# Revit family: KORO
name_source: partatom
category: Luminaires
units: mm (PartAtom-declared; Revit-internal decimal feet)

## family parameters
Cote de connecteur circulaire = Utiliser le diamètre
Couper avec des vides une fois chargée = Oui
Hôte = Face
Numéro OmniClass = 23.80.70.11.17
Partagée = Non
Point de calcul de pièce = Oui
Source d'éclairage = Oui
Titre OmniClass = Specialized Lighting by Location or Use
Type d'élément = Normal

## types (1)
- 621400
    Angle de l'inclinaison = 60.00°
    Charge apparente = 38 VA
    Commentaires relatifs à la puissance = 36.5W
    Coût = 167.5 $
    Description = Encastré tertiaire équipé de platines LED, efficacité lumineuse de 133.8lm/W
    Distance bord corps = 24 mm  [stored 0.0787402 ft]
    Distance diffuseur/diffuseur = 24 mm  [stored 0.0787402 ft]
    Elévation par défaut = 0 mm  [stored 0 ft]
    Emettre à partir de la longueur de la ligne = 610 mm
    Fabricant = Résistex
    Fichier de distribution photométrique = 621400.ies
    Filtre de couleur = 16777215
    Garantie = 5 ans
    Gradation des changements de température de couleur de lampe = <Aucun>
    IK = 04
    IP = 40
    Image du type = <Aucun>
    Indice de charge = Eclairage
    Largeur = 295 mm  [stored 0.967848 ft]
    Largeur diffuseur = 79 mm  [stored 0.259186 ft]
    Longueur = 1195 mm  [stored 3.9206 ft]
    Longueur diffuseur = 562 mm  [stored 1.84383 ft]
    Matériau corps = Alu blanc
    Matériau diffuseur = PC Transparent
    Modèle = Koro
    Nombre pôles = 2
    Tension = 230 V
    URL = https://www.resistex-sa.com
    Épaisseur = 20 mm  [stored 0.0656168 ft]

note: [stored X ft] marks values corroborated as IEEE doubles in the binary element streams (Revit-internal decimal feet)
